# Revit family: Беседка стальная «Физалес» Арт 11285
name_source: partatom
category: Антураж
revit_build: Autodesk Revit 2018 (Build: 20180423_1000(x64)
units: mm (PartAtom-declared; Revit-internal decimal feet)

## family parameters
Всегда вертикально = Да
Источник визуального образа = Геометрия семейства
На основе рабочей плоскости = Нет
Общий = Нет
При загрузке вырезать с полостями = Нет
Точка расчета площади = Нет

## types (2) — shared parameters
URL = https://hobbyka.ru
Артикул товара = Арт. 11285
Высота = 3400 мм
Группа модели = Навесы и беседки
Диаметр = 4240 мм
Длина = 4240 мм
Изготовитель = ООО «Хоббика»
Материал изделия = Сталь, чугун, дерево, мягкая черепица
Цвет каркаса = Сталь
Цвет крыши = Крыша
Цвет опоры лавки = Сталь
Цвет сидения лавки = Дерево
Ширина = 4240 мм

## per-type parameters (varying)
| type | Изображение типоразмера | Скамейка |
| Беседка стальная «Физалес», без скамейки | Беседка стальная «Физалес» без скамейки Арт 11285.jpg | Нет |
| Беседка стальная «Физалес», со скамейкой | Беседка стальная «Физалес» со скамейкой Арт 11285.jpg | Да |

note: column(s) folded — value = type name in every type: Описание
